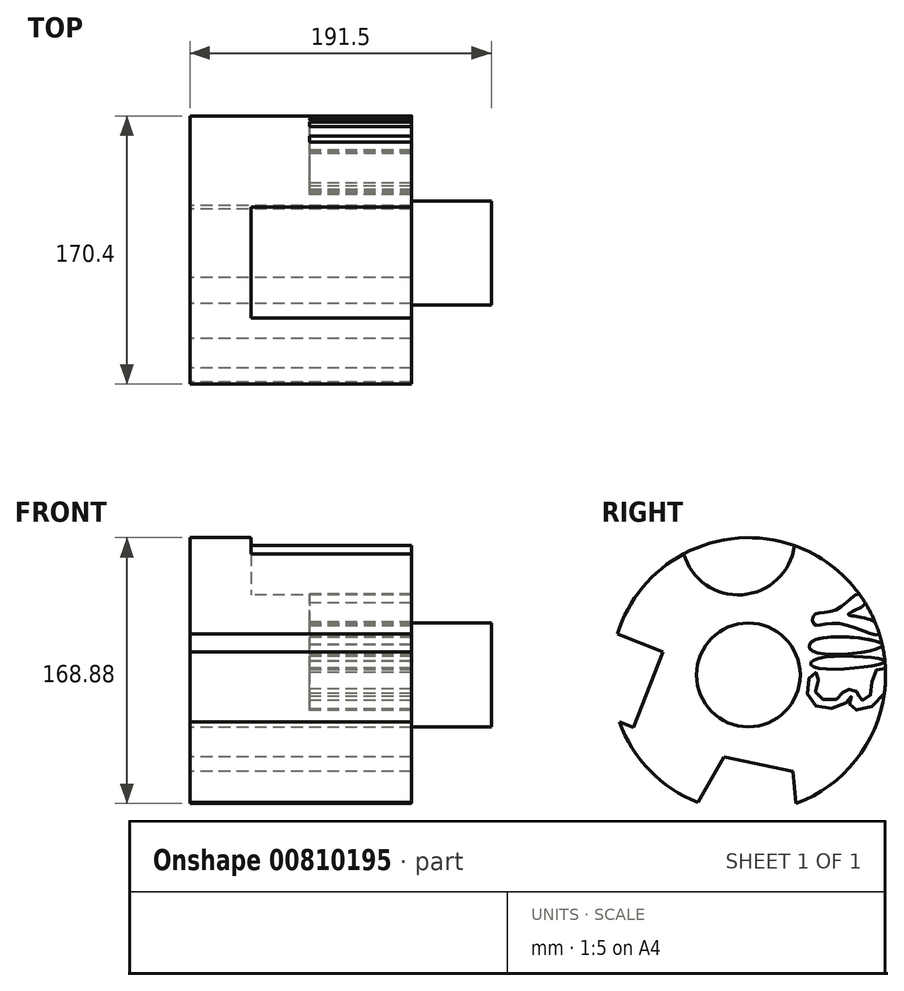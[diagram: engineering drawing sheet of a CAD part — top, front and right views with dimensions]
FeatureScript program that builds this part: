
annotation { "Feature Type Name" : "Feature", "Feature Type Description" : "" }
export const myFeature = defineFeature(function(context is Context, id is Id, definition is map)
    precondition{}
    {
        {
            var Q0;
            Q0=qCreatedBy(makeId("Right.planeOp"),FACE);
            var sketch = newSketch(context, id + "F0", { "sketchPlane" : qUnion([Q0])});
            skCircle(sketch, "E0", {"center": v(0, 0) * mm, "radius": 32.93 * mm});
            skSolve(sketch);
        }
        {
            var Q0;
            Q0=makeQuery(id+"F0.imprint","IMPRINT",FACE,{"disambiguationData":[TD([[makeQuery(id+"F0.imprint","IMPRINT",EDGE,{"derivedFrom":sQuery(id+"F0.wireOp",EDGE,"E0")}),1.0]])]});
            extrude(context, id + "F1", {"entities" : qUnion([Q0]), "depth" : 101.5 * mm, "offsetDistance" : 25 * mm});
        }
        {
            var Q0;
            Q0=qCreatedBy(makeId("Right.planeOp"),FACE);
            var sketch = newSketch(context, id + "F2", { "sketchPlane" : qUnion([Q0])});
            skCircle(sketch, "E1", {"center": v(0, 0) * mm, "radius": 87.16 * mm});
            skCircle(sketch, "E2", {"center": v(-6.45, 86.92) * mm, "radius": 36.08 * mm});
            skSolve(sketch);
        }
        {
            var Q0;
            {var subQ0=sQuery(id+"F2.wireOp",EDGE,"E2");var subQ1=sQuery(id+"F2.wireOp",EDGE,"E1");var subQ2=makeQuery(id+"F2.imprint","INTERSECT",VERTEX,{"disambiguationData":[OD(0.0)],"derivedFrom":[subQ1,subQ0]});Q0=makeQuery(id+"F2.imprint","IMPRINT",FACE,{"disambiguationData":[TD([[makeQuery(id+"F2.imprint","IMPRINT",EDGE,{"disambiguationData":[TD([[subQ2,-1.0]])],"derivedFrom":subQ1}),1.0]])]});}
            var sketch = newSketch(context, id + "F3", { "sketchPlane" : qUnion([Q0])});
            skCircle(sketch, "E3.cCircle", {"center": v(0, -86.79) * mm, "radius": 37.94 * mm, "construction": true});
            skLineSegment(sketch, "E3.0", {"start": v(-37.72, -90.8) * mm, "end": v(-15.47, -52.15) * mm});
            skLineSegment(sketch, "E3.1", {"start": v(-15.47, -52.15) * mm, "end": v(28.16, -61.36) * mm});
            skLineSegment(sketch, "E3.2", {"start": v(28.16, -61.36) * mm, "end": v(32.88, -105.71) * mm});
            skLineSegment(sketch, "E3.3", {"start": v(32.88, -105.71) * mm, "end": v(-7.84, -123.9) * mm});
            skLineSegment(sketch, "E3.4", {"start": v(-7.84, -123.9) * mm, "end": v(-37.72, -90.8) * mm});
            skCircle(sketch, "E4.cCircle", {"center": v(-87.6, 0) * mm, "radius": 36.36 * mm, "construction": true});
            skLineSegment(sketch, "E4.0", {"start": v(-102.35, 33.24) * mm, "end": v(-54.36, 14.74) * mm});
            skLineSegment(sketch, "E4.1", {"start": v(-54.36, 14.74) * mm, "end": v(-72.86, -33.24) * mm});
            skLineSegment(sketch, "E4.2", {"start": v(-72.86, -33.24) * mm, "end": v(-120.84, -14.74) * mm});
            skLineSegment(sketch, "E4.3", {"start": v(-120.84, -14.74) * mm, "end": v(-102.35, 33.24) * mm});
            skSolve(sketch);
        }
        {
            var Q0;
            {var subQ9=sQuery(id+"F3.wireOp",EDGE,"E3.1");Q0=makeQuery(id+"F3.imprint","IMPRINT",FACE,{"disambiguationData":[TD([[makeQuery(id+"F3.imprint","IMPRINT",EDGE,{"derivedFrom":subQ9}),1.0]])]});}
            extrude(context, id + "F4", {"entities" : qUnion([Q0]), "operationType" : NewBodyOperationType.ADD, "depth" : 76 * mm, "offsetDistance" : 25 * mm});
        }
        {
            var Q0;
            {var subQ0=sQuery(id+"F2.wireOp",EDGE,"E2");var subQ1=sQuery(id+"F2.wireOp",EDGE,"E1");var subQ2=makeQuery(id+"F2.imprint","INTERSECT",VERTEX,{"disambiguationData":[OD(0.0)],"derivedFrom":[subQ1,subQ0]});Q0=makeQuery(id+"F2.imprint","IMPRINT",FACE,{"disambiguationData":[TD([[makeQuery(id+"F2.imprint","IMPRINT",EDGE,{"disambiguationData":[TD([[subQ2,1.0]])],"derivedFrom":subQ1}),1.0]])]});}
            extrude(context, id + "F5", {"entities" : qUnion([Q0]), "operationType" : NewBodyOperationType.ADD, "depth" : 39 * mm, "offsetDistance" : 25 * mm});
        }
        {
            var Q0;
            Q0=makeQuery(id+"F4.opExtrude","CAP_FACE",FACE,{"disambiguationData":[OSD([sQuery(id+"F2.wireOp",EDGE,"E1"),sQuery(id+"F2.wireOp",EDGE,"E2"),sQuery(id+"F3.wireOp",EDGE,"E3.0"),sQuery(id+"F3.wireOp",EDGE,"E3.1"),sQuery(id+"F3.wireOp",EDGE,"E3.2"),sQuery(id+"F3.wireOp",EDGE,"E4.0"),sQuery(id+"F3.wireOp",EDGE,"E4.1"),sQuery(id+"F3.wireOp",EDGE,"E4.2")])],"isStart":false});
            var sketch = newSketch(context, id + "F6", { "sketchPlane" : qUnion([Q0])});
            skFitSpline(sketch, "E5", {"points": [v(80.41, 33.63) * mm, v(63.58, 38.54) * mm, v(74.26, 45.65) * mm, v(70.4, 51.39) * mm, v(56.08, 41.48) * mm, v(41.87, 38.07) * mm, v(41.9, 32.12) * mm, v(57.43, 32.69) * mm, v(83.28, 25.74) * mm, v(80.41, 33.63) * mm]});
            skFitSpline(sketch, "E6", {"points": [v(85.07, 18.98) * mm, v(41.58, 21.89) * mm, v(41.52, 14.86) * mm, v(85.07, 18.98) * mm]});
            skFitSpline(sketch, "E7", {"points": [v(86.73, 8.66) * mm, v(41.52, 9.5) * mm, v(41.52, 5.06) * mm, v(86.73, 8.66) * mm]});
            skFitSpline(sketch, "E8", {"points": [v(87.5, 3.62) * mm, v(81.9, -17.7) * mm, v(64.65, -20.25) * mm, v(65.43, -13.84) * mm, v(59.3, -19.43) * mm, v(38.92, -16.25) * mm, v(41.13, 1.36) * mm, v(44.58, -0.62) * mm, v(43.08, -12.63) * mm, v(56.56, -15.1) * mm, v(61.41, -9.38) * mm, v(67.04, -9.96) * mm, v(70.26, -11.64) * mm, v(70.46, -15.44) * mm, v(76.76, -14.2) * mm, v(79.84, 1.43) * mm, v(87.5, 3.62) * mm]});
            skSolve(sketch);
        }
        {
            var Q0;
            Q0=makeQuery(id+"F1.opExtrude","CAP_FACE",FACE,{"disambiguationData":[OSD([sQuery(id+"F0.wireOp",EDGE,"E0")])],"isStart":false});
            extrude(context, id + "F7", {"entities" : qUnion([Q0]), "operationType" : NewBodyOperationType.ADD, "depth" : 90 * mm, "offsetDistance" : 25 * mm});
        }
        {
            var Q0;
            {var subQ0=sQuery(id+"F6.wireOp",EDGE,"E5");var subQ1=sQuery(id+"F2.wireOp",EDGE,"E2");var subQ2=sQuery(id+"F2.wireOp",EDGE,"E1");var subQ3=makeQuery(id+"F2.imprint","INTERSECT",VERTEX,{"disambiguationData":[OD(0.0)],"derivedFrom":[subQ2,subQ1]});var subQ5=makeQuery(id+"F2.imprint","IMPRINT",EDGE,{"disambiguationData":[TD([[subQ3,-1.0]])],"derivedFrom":subQ2});var subQ6=makeQuery(id+"F4.opExtrude","CAP_EDGE",EDGE,{"disambiguationData":[OSD([subQ2]),TDD([makeQuery(id+"F3.imprint","IMPRINT",EDGE,{"disambiguationData":[TD([[makeQuery(id+"F3.imprint","INTERSECT",VERTEX,{"derivedFrom":[subQ5,sQuery(id+"F3.wireOp",EDGE,"E3.2")]}),-1.0]])],"derivedFrom":subQ5})])],"isStart":false});var subQ7=makeQuery(id+"F6.imprint","INTERSECT",VERTEX,{"disambiguationData":[OD(0.0)],"derivedFrom":[subQ6,subQ0]});Q0=makeQuery(id+"F6.imprint","IMPRINT",FACE,{"disambiguationData":[TD([[makeQuery(id+"F6.imprint","IMPRINT",EDGE,{"disambiguationData":[TD([[subQ7,1.0]])],"derivedFrom":subQ0}),-1.0]])]});}
            var Q1;
            {var subQ5=sQuery(id+"F3.wireOp",EDGE,"E3.0");Q1=makeQuery(id+"F6.imprint","IMPRINT",FACE,{"disambiguationData":[TD([[makeQuery(id+"F6.imprint","IMPRINT",EDGE,{"derivedFrom":makeQuery(id+"F4.opExtrude","CAP_EDGE",EDGE,{"disambiguationData":[OSD([subQ5])],"isStart":false})}),1.0]])]});}
            extrude(context, id + "F8", {"entities" : qUnion([Q0, Q1]), "operationType" : NewBodyOperationType.ADD, "depth" : 64.8 * mm, "offsetDistance" : 25 * mm});
        }
    });
